# Revit family: Artek_Benches_Kiki Bench_Kiki Bench 2-seater
name_source: partatom
category: Furniture
revit_build: Autodesk Revit 2017 (Build: 20160225_1515(x64)
units: mm (PartAtom-declared; Revit-internal decimal feet)

## family parameters
Always vertical = Yes
Cut with Voids When Loaded = No
OmniClass Number = 23.40.20.14.14.21
OmniClass Title = Benches
Room Calculation Point = No
Shared = No
Work Plane-Based = No

## types (1)
- Kiki Bench 2-seater
    AssetType = Movable
    BIMObjectName = Artek_Benches_Kiki Bench_Kiki Bench 2-seater
    Brand = Artek
    Category = Benches
    Collection = Kiki Collection
    Color = Black
    ConvergoRefNr = 0190-2009-0043-FI
    Cost = 0 $
    Designer = Ilmari Tapiovaara
    DurationUnit = Years
    HighestSeatingHeight = 399 mm
    IfcExportAs = IfcFurnishingElementType
    IfcExportType = BENCH
    LegsMaterial = Powder coated black metal
    LowestSeatingHeight = 399 mm
    MainColor = Black
    Manufacturer = Artek
    ManufacturerName = Artek
    ManufacturerURL = https://www.artek.fi
    Material = Steel tubing/Upholstery
    Model = Kiki Bench 2-seater
    ModelNumber = 28501102
    NBSDescription = Benches
    NBSReference = 45-35-86/321
    Name = Kiki Bench 2-seater
    NominalDepth = 553 mm
    NominalHeight = 399 mm
    NominalLength = 1169 mm
    SeatingHeight = 399 mm
    Shape = Sculptured
    Size = 1160x390x540 mm
    URL = https://www.artek.fi
    Uniclass2 = Pr_40_50_12
    Uniclass2015Description = Chairs, seats and benches
    Uniclass2015Reference = Pr_40_50_12
    Version = 1
    VersionDate = 11/3/2020
    WarrantyDurationUnit = Years

## geometry (parser evidence)
native form markers: Sweep x4
no freeform markers — native parametric forms only
